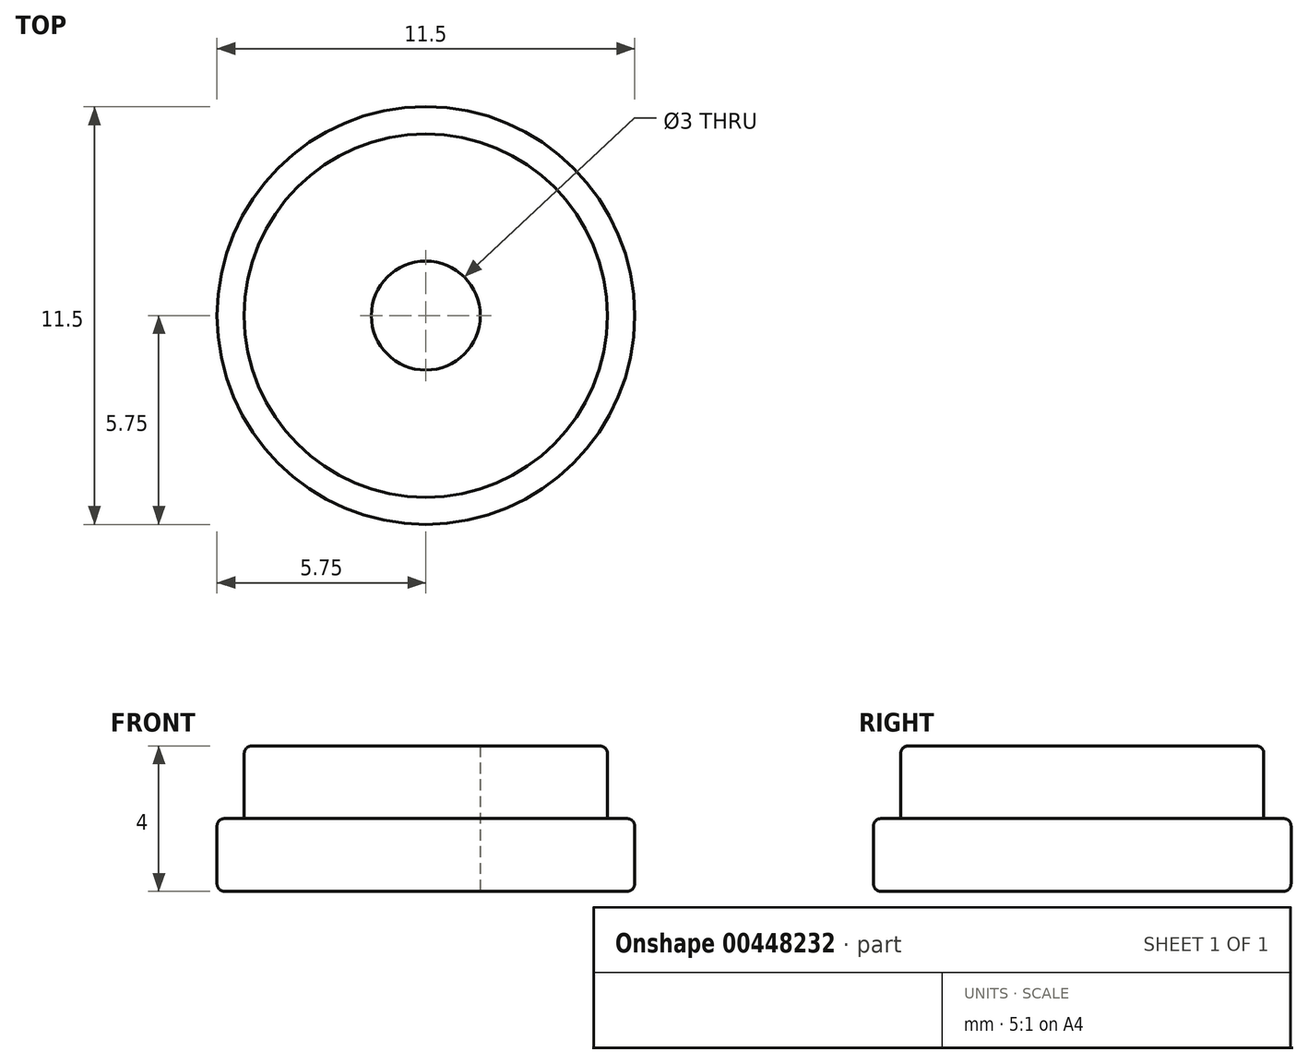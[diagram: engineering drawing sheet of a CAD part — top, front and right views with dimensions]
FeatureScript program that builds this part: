
annotation { "Feature Type Name" : "Feature", "Feature Type Description" : "" }
export const myFeature = defineFeature(function(context is Context, id is Id, definition is map)
    precondition{}
    {
        {
            var Q0;
            Q0=qCreatedBy(makeId("Top.planeOp"),FACE);
            var sketch = newSketch(context, id + "F0", { "sketchPlane" : qUnion([Q0])});
            skCircle(sketch, "E0", {"center": v(0, 0) * mm, "radius": 5 * mm});
            skCircle(sketch, "E1", {"center": v(0, 0) * mm, "radius": 5.75 * mm});
            skCircle(sketch, "E2", {"center": v(0, 0) * mm, "radius": 1.5 * mm});
            skSolve(sketch);
        }
        {
            var Q0;
            Q0=makeQuery(id+"F0.imprint","IMPRINT",FACE,{"disambiguationData":[TD([[makeQuery(id+"F0.imprint","IMPRINT",EDGE,{"derivedFrom":sQuery(id+"F0.wireOp",EDGE,"E0")}),1.0]])]});
            extrude(context, id + "F1", {"entities" : qUnion([Q0]), "depth" : 4 * mm});
        }
        {
            var Q0;
            Q0 = qSketchRegion(id + "F0", true);
            extrude(context, id + "F2", {"entities" : qUnion([Q0]), "operationType" : NewBodyOperationType.ADD, "depth" : 2 * mm});
        }
        {
            var Q0;
            Q0=makeQuery(id+"F1.opExtrude","CAP_EDGE",EDGE,{"disambiguationData":[OSD([sQuery(id+"F0.wireOp",EDGE,"E0")])],"isStart":false});
            var Q1;
            Q1=makeQuery(id+"F2.opExtrude","CAP_EDGE",EDGE,{"disambiguationData":[OSD([sQuery(id+"F0.wireOp",EDGE,"E1")])],"isStart":false});
            var Q2;
            Q2=makeQuery(id+"F2.opExtrude","CAP_EDGE",EDGE,{"disambiguationData":[OSD([sQuery(id+"F0.wireOp",EDGE,"E1")])],"isStart":true});
            fillet(context, id + "F3", {"entities" : qUnion([Q0, Q1, Q2]), "radius" : 0.2 * mm, "tangentPropagation" : true, "allowEdgeOverflow" : false});
        }
    });
